# Revit family: KKDC_General_KOH40-R_HighCRI_3000K_1140mm
name_source: partatom
category: 조명 설비
units: mm (PartAtom-declared; Revit-internal decimal feet)

## family parameters
OmniClass 번호 = 23.80.70.00
OmniClass 제목 = Lighting
공유 = 아니오
광원 = 예
로드될 때 보이드를 사용하여 절단 = 예
룸 계산 점 = 아니오
부품 유형 = 배선함
원형 커넥터 치수 = 지름 사용
작업 기준면 기반 = 예
주석 방향 유지 = 아니오
항상 수직 = 예

## types (3) — shared parameters
감광 램프 색상 온도 변화 = <없음>
경사도 = 90.00°
기본 높이 = 1219.2  [stored 4 ft]
램프 = KOH40 HighCRI
렌더링 시 발산 모양 표시 = 예
색상 필터 = 16777215
와티지 해설 = 35W/m
직사각형 길이에서 발산 = 1140  [stored 3.74016 ft]
직사각형 폭에서 발산 = 40  [stored 0.131234 ft]

## per-type parameters (varying)
| type | 측광 웹 파일 |
| KOH40-R HighCRI 3000K Diffused 1140mm | KOH40 HighCRI Diffuesd.IES |
| KOH40-R HighCRI 3000K Louvre Frosted 1140mm | KOH40 HighCRI Louvre Frosted.IES |
| KOH40-R HighCRI 3000K Prismatic 1140mm | KOH40 HighCRI Prismatic.IES |

note: [stored X ft] marks values corroborated as IEEE doubles in the binary element streams (Revit-internal decimal feet)
